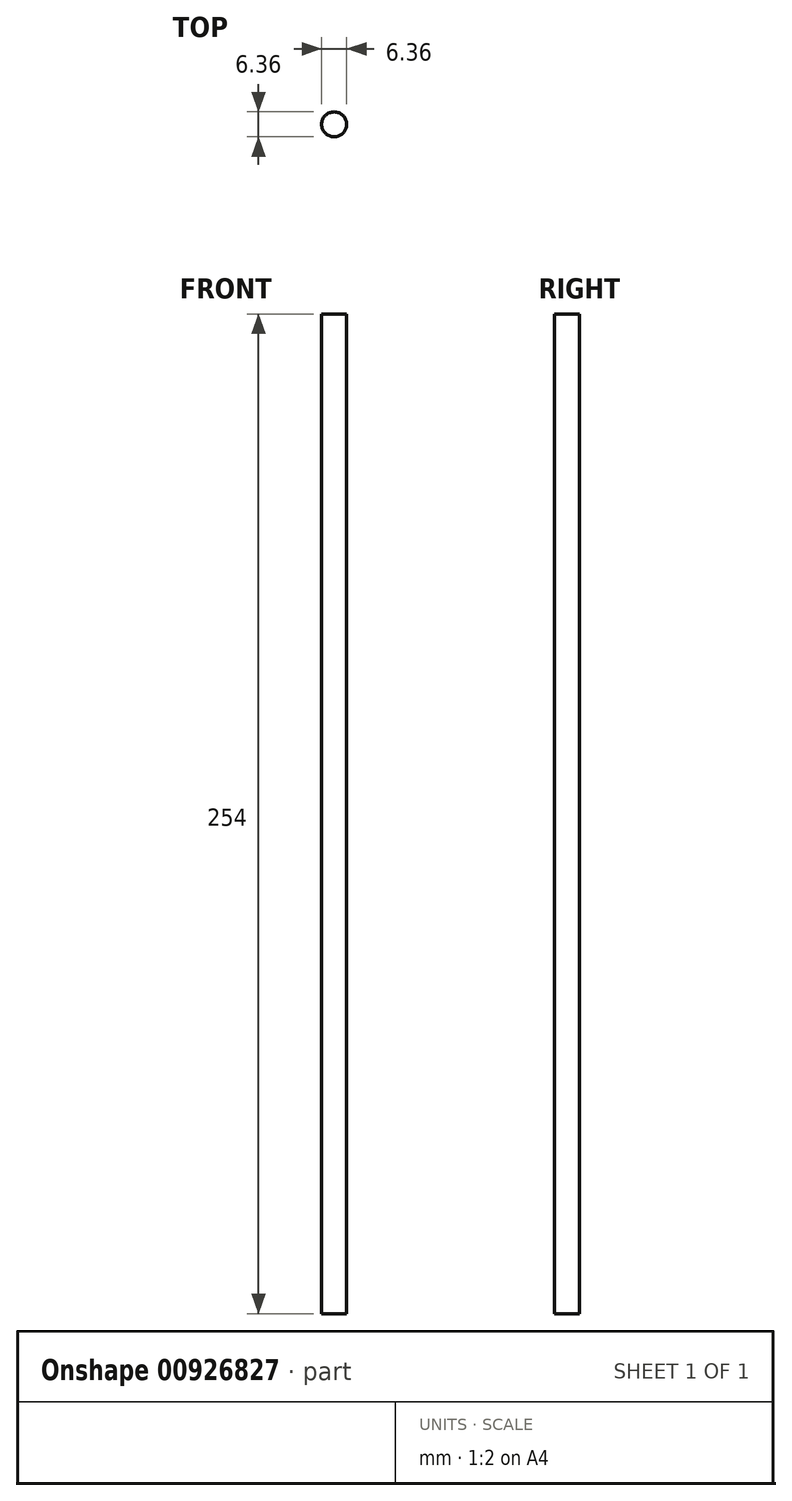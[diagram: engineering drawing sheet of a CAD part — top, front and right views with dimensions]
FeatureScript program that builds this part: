
annotation { "Feature Type Name" : "Feature", "Feature Type Description" : "" }
export const myFeature = defineFeature(function(context is Context, id is Id, definition is map)
    precondition{}
    {
        {
            var Q0;
            Q0=qCreatedBy(makeId("Top.planeOp"),FACE);
            var sketch = newSketch(context, id + "F0", { "sketchPlane" : qUnion([Q0])});
            skCircle(sketch, "E0", {"center": v(0, 0) * mm, "radius": 3.18 * mm});
            skSolve(sketch);
        }
        {
            var Q0;
            Q0 = qSketchRegion(id + "F0", true);
            extrude(context, id + "F1", {"entities" : qUnion([Q0]), "depth" : 254 * mm, "offsetDistance" : 25.4 * mm});
        }
    });
